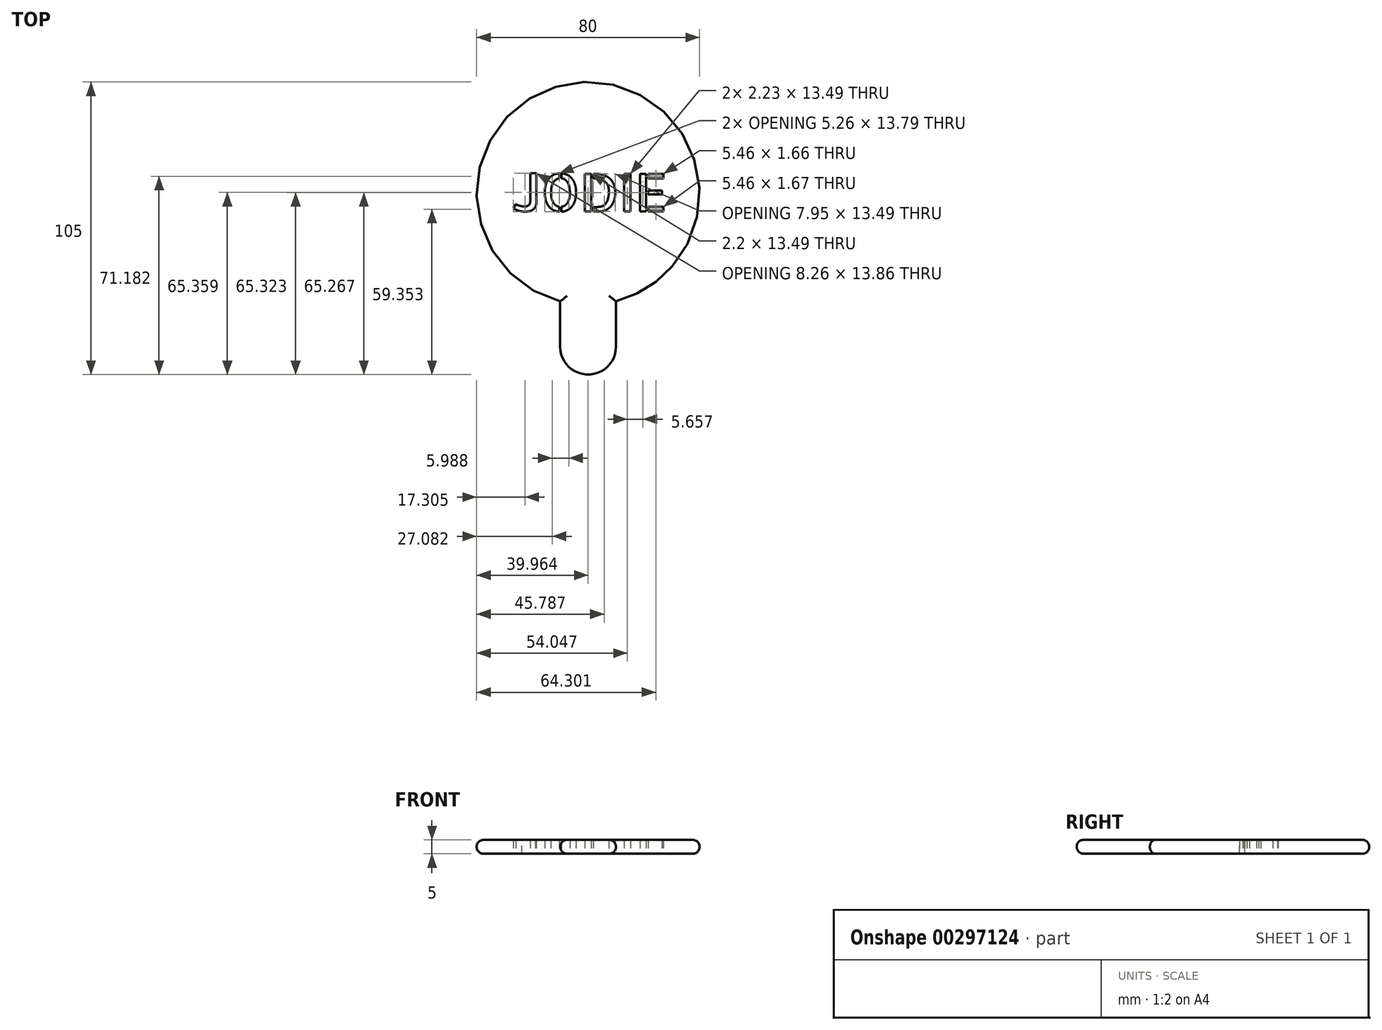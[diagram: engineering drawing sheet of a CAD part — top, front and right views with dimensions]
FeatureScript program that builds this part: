
annotation { "Feature Type Name" : "Feature", "Feature Type Description" : "" }
export const myFeature = defineFeature(function(context is Context, id is Id, definition is map)
    precondition{}
    {
        {
            var Q0;
            Q0=qCreatedBy(makeId("Top.planeOp"),FACE);
            var sketch = newSketch(context, id + "F0", { "sketchPlane" : qUnion([Q0])});
            skCircle(sketch, "E0", {"center": v(0, 0) * mm, "radius": 40 * mm});
            skText(sketch, "E1", { "text": "JODIE", "fontName": "AllertaStencil-Regular.ttf"});
            const initialGuessF0  = {"E1": [-0.0273, -0.00648, 1, 0, 0.0135]};
            skSetInitialGuess(sketch, initialGuessF0);
            skSolve(sketch);
        }
        {
            var Q0;
            Q0 = qSketchRegion(id + "F0", true);
            extrude(context, id + "F1", {"entities" : qUnion([Q0]), "depth" : 5 * mm});
        }
        {
            var Q0;
            Q0=qCreatedBy(makeId("Top.planeOp"),FACE);
            var sketch = newSketch(context, id + "F2", { "sketchPlane" : qUnion([Q0])});
            skLineSegment(sketch, "E2.bottom", {"start": v(-10, -65) * mm, "end": v(10, -65) * mm});
            skLineSegment(sketch, "E2.top", {"start": v(-10, 65) * mm, "end": v(10, 65) * mm});
            skLineSegment(sketch, "E2.left", {"start": v(-10, -65) * mm, "end": v(-10, 65) * mm});
            skLineSegment(sketch, "E2.right", {"start": v(10, -65) * mm, "end": v(10, 65) * mm});
            skPoint(sketch, "E2.middle", {"position": v(0, 0) * mm});
            skLineSegment(sketch, "E3", {"start": v(-10, -31.18) * mm, "end": v(10, -31.18) * mm});
            skSolve(sketch);
        }
        {
            var Q0;
            {var subQ0=sQuery(id+"F2.wireOp",EDGE,"E2.bottom");Q0=makeQuery(id+"F2.imprint","IMPRINT",FACE,{"disambiguationData":[TD([[makeQuery(id+"F2.imprint","IMPRINT",EDGE,{"derivedFrom":subQ0}),1.0]])]});}
            extrude(context, id + "F3", {"entities" : qUnion([Q0]), "operationType" : NewBodyOperationType.ADD, "depth" : 5 * mm});
        }
        {
            var Q0;
            Q0=makeQuery(id+"F3.opExtrude","SWEPT_EDGE",EDGE,{"disambiguationData":[OSD([sQuery(id+"F2.wireOp",EDGE,"E2.bottom"),sQuery(id+"F2.wireOp",EDGE,"E2.left")])]});
            var Q1;
            Q1=makeQuery(id+"F3.opExtrude","SWEPT_EDGE",EDGE,{"disambiguationData":[OSD([sQuery(id+"F2.wireOp",EDGE,"E2.bottom"),sQuery(id+"F2.wireOp",EDGE,"E2.right")])]});
            fillet(context, id + "F4", {"entities" : qUnion([Q0, Q1]), "radius" : 10 * mm, "tangentPropagation" : true, "allowEdgeOverflow" : false});
        }
        {
            var Q0;
            Q0=makeQuery(id+"F1.opExtrude","CAP_EDGE",EDGE,{"disambiguationData":[OSD([sQuery(id+"F0.wireOp",EDGE,"E0")])],"isStart":false});
            var Q1;
            Q1=makeQuery(id+"F3.opExtrude","CAP_EDGE",EDGE,{"disambiguationData":[OSD([sQuery(id+"F2.wireOp",EDGE,"E2.left")])],"isStart":false});
            fillet(context, id + "F5", {"entities" : qUnion([Q0, Q1]), "radius" : 2.5 * mm, "tangentPropagation" : true, "allowEdgeOverflow" : false});
        }
        {
            var Q0;
            Q0=makeQuery(id+"F1.opExtrude","CAP_EDGE",EDGE,{"disambiguationData":[OSD([sQuery(id+"F0.wireOp",EDGE,"E0")])],"isStart":true});
            var Q1;
            Q1=makeQuery(id+"F3.opExtrude","CAP_EDGE",EDGE,{"disambiguationData":[OSD([sQuery(id+"F2.wireOp",EDGE,"E2.left")])],"isStart":true});
            fillet(context, id + "F6", {"entities" : qUnion([Q0, Q1]), "radius" : 2.5 * mm, "tangentPropagation" : true, "allowEdgeOverflow" : false});
        }
    });
